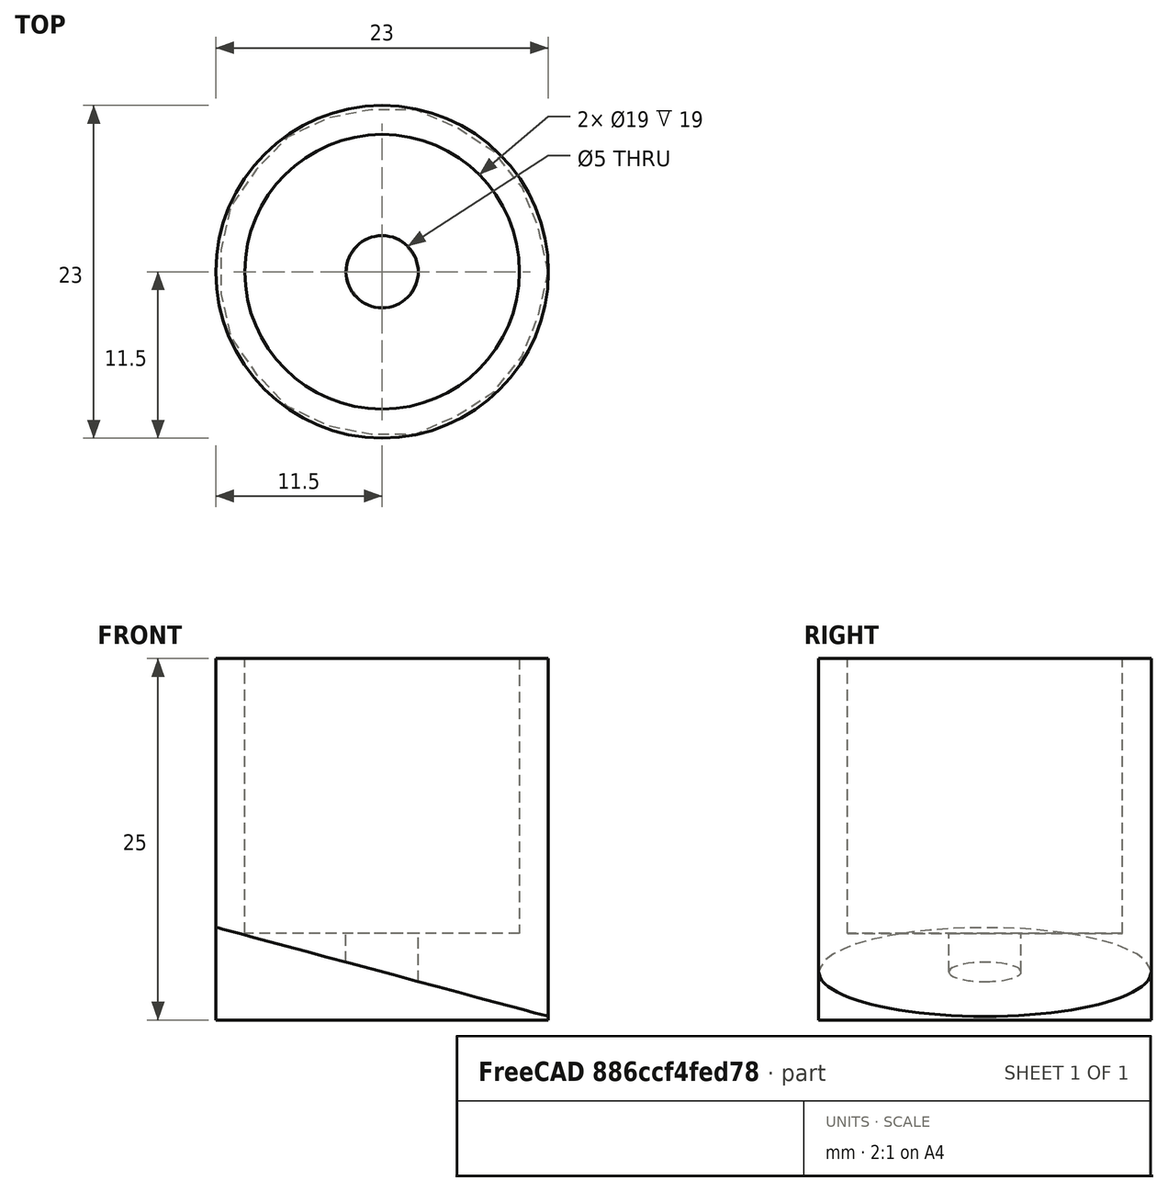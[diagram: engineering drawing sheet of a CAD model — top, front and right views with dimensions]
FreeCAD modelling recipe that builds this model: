
FCSTD DOCUMENT  (FreeCAD 0.19R)
Label: 18650Tube
License: All rights reserved
LicenseURL: http://en.wikipedia.org/wiki/All_rights_reserved
objects: Sketcher::SketchObject×2, Part::Cut×2, PartDesign::Pad×1, PartDesign::Pocket×1, PartDesign::Body×1, Part::Box×1, Part::Cylinder×1, Mesh::Feature×1
note: 11 computed .brp shape members not serialized (recipe doc carries the construction recipe); baked Part::Feature solids carry a one-line shape summary decoded from their .brp

FEATURE [Sketcher::SketchObject] Sketch
  FullyConstrained = true
  MapMode = 5
  Support = -> [XY_Plane]
  sketch-geometry (1):
    g0: Circle CenterX=0 CenterY=0 CenterZ=0 NormalX=0 NormalY=0 NormalZ=1 AngleXU=0 Radius=11.5
  constraints (2):
    c: Coincident(g0,g-1)
    c: Diameter(g0) = 23
FEATURE [PartDesign::Pad] Pad
  Direction = (1,1,1)
  Length = 25
  Length2 = 100
  Profile = -> Sketch
  Type = 0
FEATURE [Sketcher::SketchObject] Sketch001
  FullyConstrained = true
  MapMode = 5
  Placement = pos=(0,0,25) rot=(0,0,1;0rad)
  Support = -> [Pad]
  sketch-geometry (1):
    g0: Circle CenterX=0 CenterY=0 CenterZ=0 NormalX=0 NormalY=0 NormalZ=1 AngleXU=0 Radius=9.5
  constraints (2):
    c: Coincident(g0,g-1)
    c: Diameter(g0) = 19
FEATURE [PartDesign::Pocket] Pocket
  BaseFeature = -> Pad
  Length = 19
  Length2 = 100
  Profile = -> Sketch001
  Type = 0
FEATURE [PartDesign::Body] Body
  Group = -> [Sketch,Pad,Sketch001,Pocket]
  Origin = -> Origin
  Tip = -> Pocket
FEATURE [Part::Box] Box  label="Cube"
  AttacherType = Attacher::AttachEngine3D
  Height = 100
  Length = 100
  Placement = pos=(-53,-53,-86) rot=(0,1,0;0.261799rad)
  Width = 100
FEATURE [Part::Cut] Cut
  Base = -> Pocket
  Tool = -> Box
FEATURE [Part::Cylinder] Cylinder
  Angle = 360
  AttacherType = Attacher::AttachEngine3D
  Height = 10
  Radius = 2.5
FEATURE [Part::Cut] Cut001
  Base = -> Cut
  Tool = -> Cylinder
FEATURE [Mesh::Feature] Mesh  label="Cut001 (Meshed)"
